# Revit family: Sanitary_Accessories_Johnson-Suisse_Swift_Robe_Hook
name_source: partatom
category: Plumbing Fixtures
revit_build: Autodesk Revit 2015 (Build: 20140606_1530(x64)
units: mm (PartAtom-declared; Revit-internal decimal feet)

## types (1)
- Swift Robe Hook
    BIMobject category = Accessories
    Brand url = http://www.johnsonsuisse.com.au
    Design country = Spain
    EAN code = https://9325304004594
    Edition number = 1
    IFC Classification = Furnishing Element
    Manufacturer country = China
    Manufacturer name = Johnson Suisse
    Material main = Metal
    Material secondary = Chrome
    NBS Reference Code = 35-75-18
    NBS Reference Description = Clothes Hooks
    Nominal height = 55 mm  [stored 0.180446 ft]
    Nominal width = 55 mm  [stored 0.180446 ft]
    Product Guid = 3c7373e0-a690-4978-ad7b-8ef91a4ea9e1
    Product SKU = GDC150121
    Product data url = https://bimobject.com
    Product family = Swift
    Product group = Accessories
    Product url = https://johnsonsuisse.com.au
    QR code = http://bimobject.com
    Technical description = https://johnsonsuisse.com.au
    Type = swift_robe_hook : Default
    UNSPSC Code = 301815
    Uniclass 1.4 Code = L824
    Uniclass 1.4 Description = Bathroom, toilet furniture and fittings
    Uniclass 2.0 Code = PR-35-75-18
    Uniclass 2.0 Description = Clothes Hooks
    Uniclass 2015 Code = Pr_40_30_78_15
    Uniclass 2015 Name = Clothes hooks
    Weight Net (Kg) = 0.125

note: [stored X ft] marks values corroborated as IEEE doubles in the binary element streams (Revit-internal decimal feet)

## geometry (parser evidence)
native form markers: Sweep x4
no freeform markers — native parametric forms only
